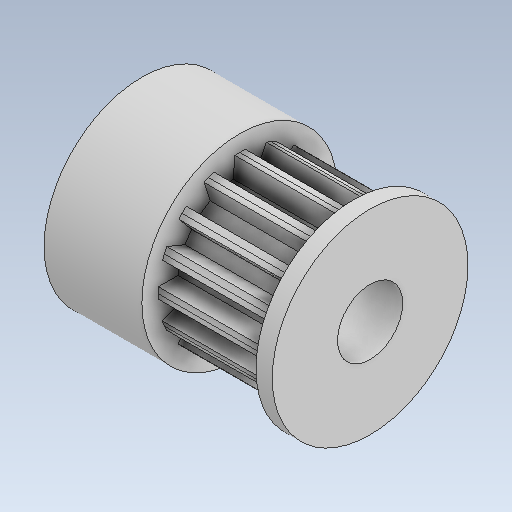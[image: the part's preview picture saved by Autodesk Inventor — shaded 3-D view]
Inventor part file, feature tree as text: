
AUTODESK INVENTOR PART (.ipt)
format: ipt  version: 2020 (Build 240168000, 168)  size: 264,192 bytes
history: native  units: mm
features: extrude x5, sketch x5, projected_geometry x3, other x1
ambient origin geometry x8: Origin, YZ Plane, XZ Plane, XY Plane, X Axis, Y Axis, Z Axis, Center Point
bodies: Body1 (feature_tree)
feature tree (14):
  other  "Твердое тело1"
  extrude  "Выдавливание1"  Depth=10.0mm
  extrude  "Выдавливание2"  Depth=7.0mm TaperAngle=0.0deg
  extrude  "Выдавливание3"  Depth=12.0mm
  extrude  "Выдавливание4"  Depth=1.0mm TaperAngle=0.0deg
  extrude  "Выдавливание5"  Depth=12.0mm
  sketch  "Эскиз1"
  sketch  "Эскиз2"
  sketch  "Эскиз3"
  sketch  "Эскиз4"
  sketch  "Эскиз5"
  projected_geometry  "Спроецированная петля1"
  projected_geometry  "Спроецированная петля2"
  projected_geometry  "Спроецированная петля3"
